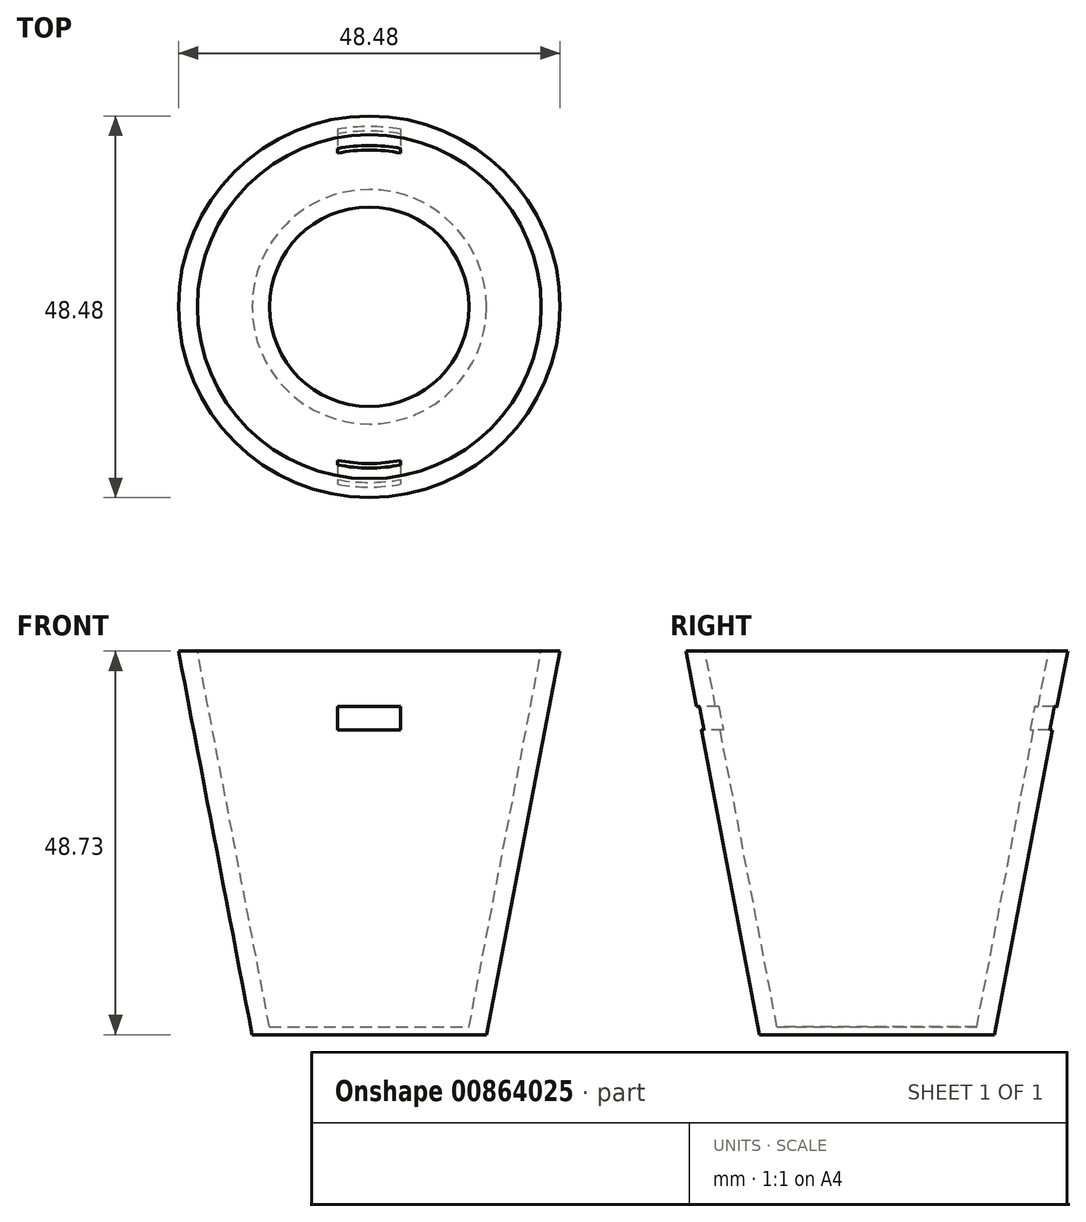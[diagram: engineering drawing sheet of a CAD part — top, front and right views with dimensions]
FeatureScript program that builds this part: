
annotation { "Feature Type Name" : "Feature", "Feature Type Description" : "" }
export const myFeature = defineFeature(function(context is Context, id is Id, definition is map)
    precondition{}
    {
        {
            var Q0;
            Q0=qCreatedBy(makeId("Front.planeOp"),FACE);
            var sketch = newSketch(context, id + "F0", { "sketchPlane" : qUnion([Q0])});
            skLineSegment(sketch, "E0", {"start": v(0, 0) * mm, "end": v(-14.9, 0) * mm});
            skLineSegment(sketch, "E1", {"start": v(-14.9, 0) * mm, "end": v(-24.24, 48.73) * mm});
            skLineSegment(sketch, "E2", {"start": v(-24.24, 48.73) * mm, "end": v(-21.84, 48.73) * mm});
            skLineSegment(sketch, "E3", {"start": v(-21.84, 48.73) * mm, "end": v(-12.68, 0.99) * mm});
            skLineSegment(sketch, "E4", {"start": v(-12.68, 0.99) * mm, "end": v(0, 0.99) * mm});
            skLineSegment(sketch, "E5", {"start": v(0, 0.99) * mm, "end": v(0, 0) * mm});
            skLineSegment(sketch, "E6", {"start": v(0, 0) * mm, "end": v(0, 43.02) * mm, "construction": true});
            skSolve(sketch);
        }
        {
            var Q0;
            Q0=makeQuery(id+"F0.imprint","IMPRINT",FACE,{"disambiguationData":[TD([[makeQuery(id+"F0.imprint","IMPRINT",EDGE,{"derivedFrom":sQuery(id+"F0.wireOp",EDGE,"E0")}),-1.0]])]});
            var Q1;
            Q1=sQuery(id+"F0.wireOp",EDGE,"E6");
            revolve(context, id + "F1", {"surfaceOperationType" : NewSurfaceOperationType.NEW, "entities" : qUnion([Q0]), "axis" : qUnion([Q1]), "revolveType" : RevolveType.FULL});
        }
        {
            var Q0;
            Q0=qCreatedBy(makeId("Front.planeOp"),FACE);
            var sketch = newSketch(context, id + "F2", { "sketchPlane" : qUnion([Q0])});
            skLineSegment(sketch, "E7", {"start": v(0, 0) * mm, "end": v(0, 61.83) * mm, "construction": true});
            skLineSegment(sketch, "E8.bottom", {"start": v(4, 38.69) * mm, "end": v(-4, 38.69) * mm});
            skLineSegment(sketch, "E8.top", {"start": v(4, 41.69) * mm, "end": v(-4, 41.69) * mm});
            skLineSegment(sketch, "E8.left", {"start": v(4, 38.69) * mm, "end": v(4, 41.69) * mm});
            skLineSegment(sketch, "E8.right", {"start": v(-4, 38.69) * mm, "end": v(-4, 41.69) * mm});
            skPoint(sketch, "E8.middle", {"position": v(0, 40.19) * mm});
            skSolve(sketch);
        }
        {
            var Q0;
            Q0 = qSketchRegion(id + "F2", true);
            extrude(context, id + "F3", {"entities" : qUnion([Q0]), "operationType" : NewBodyOperationType.REMOVE, "oppositeDirection" : true, "depth" : 500 * mm, "offsetDistance" : 25 * mm, "hasSecondDirection" : true, "secondDirectionOppositeDirection" : false, "secondDirectionDepth" : 25 * mm});
        }
    });
